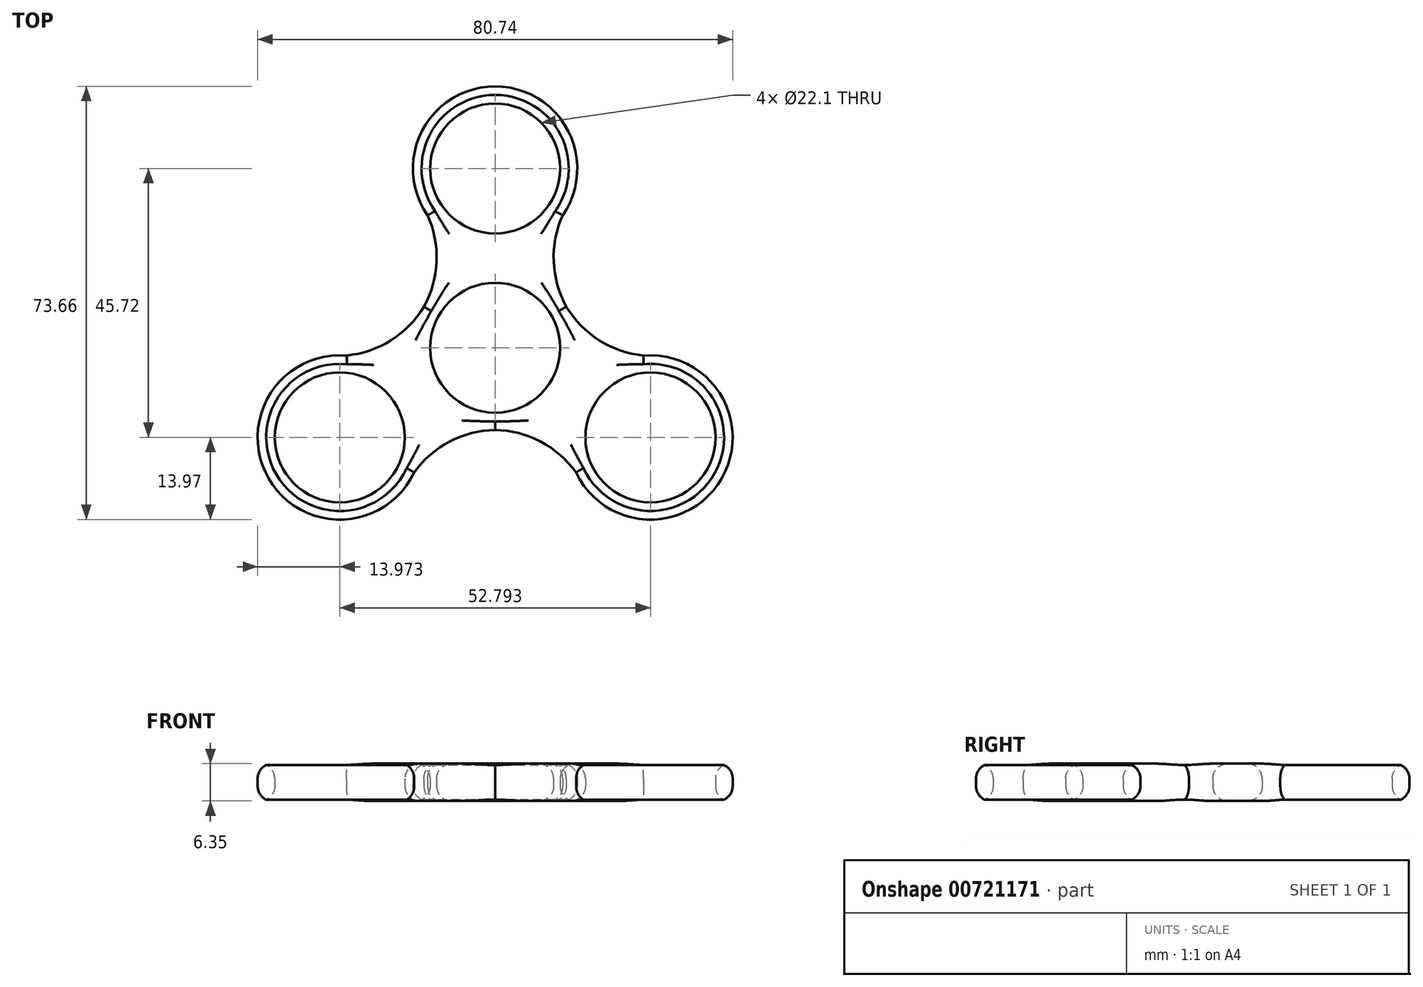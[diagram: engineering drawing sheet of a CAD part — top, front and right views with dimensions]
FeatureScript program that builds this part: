
annotation { "Feature Type Name" : "Feature", "Feature Type Description" : "" }
export const myFeature = defineFeature(function(context is Context, id is Id, definition is map)
    precondition{}
    {
        {
            var Q0;
            Q0=qCreatedBy(makeId("Top.planeOp"),FACE);
            var sketch = newSketch(context, id + "F0", { "sketchPlane" : qUnion([Q0])});
            skCircle(sketch, "E0", {"center": v(0, 0) * mm, "radius": 13.97 * mm});
            skCircle(sketch, "E1", {"center": v(0, 0) * mm, "radius": 11.05 * mm});
            skLineSegment(sketch, "E2", {"start": v(0, 0) * mm, "end": v(0, 30.48) * mm});
            skCircle(sketch, "E3", {"center": v(0, 30.48) * mm, "radius": 13.97 * mm});
            skCircle(sketch, "E4", {"center": v(0, 30.48) * mm, "radius": 11.05 * mm});
            skCircle(sketch, "E5.1.0", {"center": v(-26.4, -15.24) * mm, "radius": 11.05 * mm});
            skCircle(sketch, "E5.1.1", {"center": v(-26.4, -15.24) * mm, "radius": 13.97 * mm});
            skCircle(sketch, "E5.2.0", {"center": v(26.4, -15.24) * mm, "radius": 11.05 * mm});
            skCircle(sketch, "E5.2.1", {"center": v(26.4, -15.24) * mm, "radius": 13.97 * mm});
            skLineSegment(sketch, "E6", {"start": v(0, 0) * mm, "end": v(-26.4, 15.24) * mm});
            skArc(sketch, "E7", {"start": v(15.22, -23.62) * mm, "mid": v(8.96, -16.67) * mm, "end": v(0, -13.97) * mm});
            skArc(sketch, "E8.MirrorCS", {"start": v(-15.22, -23.62) * mm, "mid": v(-8.96, -16.67) * mm, "end": v(0, -13.97) * mm});
            skArc(sketch, "E9.1.0", {"start": v(28.06, -1.37) * mm, "mid": v(18.91, 0.57) * mm, "end": v(12.1, 6.99) * mm});
            skArc(sketch, "E9.1.1", {"start": v(12.85, 24.99) * mm, "mid": v(9.95, 16.1) * mm, "end": v(12.1, 6.99) * mm});
            skArc(sketch, "E9.2.0", {"start": v(-12.85, 24.99) * mm, "mid": v(-9.95, 16.1) * mm, "end": v(-12.1, 6.99) * mm});
            skArc(sketch, "E9.2.1", {"start": v(-28.06, -1.37) * mm, "mid": v(-18.91, 0.57) * mm, "end": v(-12.1, 6.99) * mm});
            skSolve(sketch);
        }
        {
            var Q0;
            Q0 = qSketchRegion(id + "F0", true);
            extrude(context, id + "F1", {"entities" : qUnion([Q0]), "depth" : 6.35 * mm, "offsetDistance" : 25.4 * mm});
        }
        {
            var Q0;
            Q0=makeQuery(id+"F1.opExtrude","CAP_FACE",FACE,{"disambiguationData":[OSD([sQuery(id+"F0.wireOp",EDGE,"E1"),sQuery(id+"F0.wireOp",EDGE,"E3"),sQuery(id+"F0.wireOp",EDGE,"E4"),sQuery(id+"F0.wireOp",EDGE,"E5.1.0"),sQuery(id+"F0.wireOp",EDGE,"E5.1.1"),sQuery(id+"F0.wireOp",EDGE,"E5.2.0"),sQuery(id+"F0.wireOp",EDGE,"E5.2.1"),sQuery(id+"F0.wireOp",EDGE,"E7"),sQuery(id+"F0.wireOp",EDGE,"E8.MirrorCS"),sQuery(id+"F0.wireOp",EDGE,"E9.1.0"),sQuery(id+"F0.wireOp",EDGE,"E9.1.1"),sQuery(id+"F0.wireOp",EDGE,"E9.2.0"),sQuery(id+"F0.wireOp",EDGE,"E9.2.1")])],"isStart":false});
            var Q1;
            Q1=makeQuery(id+"F1.opExtrude","CAP_FACE",FACE,{"disambiguationData":[OSD([sQuery(id+"F0.wireOp",EDGE,"E1"),sQuery(id+"F0.wireOp",EDGE,"E3"),sQuery(id+"F0.wireOp",EDGE,"E4"),sQuery(id+"F0.wireOp",EDGE,"E5.1.0"),sQuery(id+"F0.wireOp",EDGE,"E5.1.1"),sQuery(id+"F0.wireOp",EDGE,"E5.2.0"),sQuery(id+"F0.wireOp",EDGE,"E5.2.1"),sQuery(id+"F0.wireOp",EDGE,"E7"),sQuery(id+"F0.wireOp",EDGE,"E8.MirrorCS"),sQuery(id+"F0.wireOp",EDGE,"E9.1.0"),sQuery(id+"F0.wireOp",EDGE,"E9.1.1"),sQuery(id+"F0.wireOp",EDGE,"E9.2.0"),sQuery(id+"F0.wireOp",EDGE,"E9.2.1")])],"isStart":true});
            fillet(context, id + "F2", {"entities" : qUnion([Q0, Q1]), "radius" : 2.54 * mm, "tangentPropagation" : true, "allowEdgeOverflow" : false});
        }
    });
